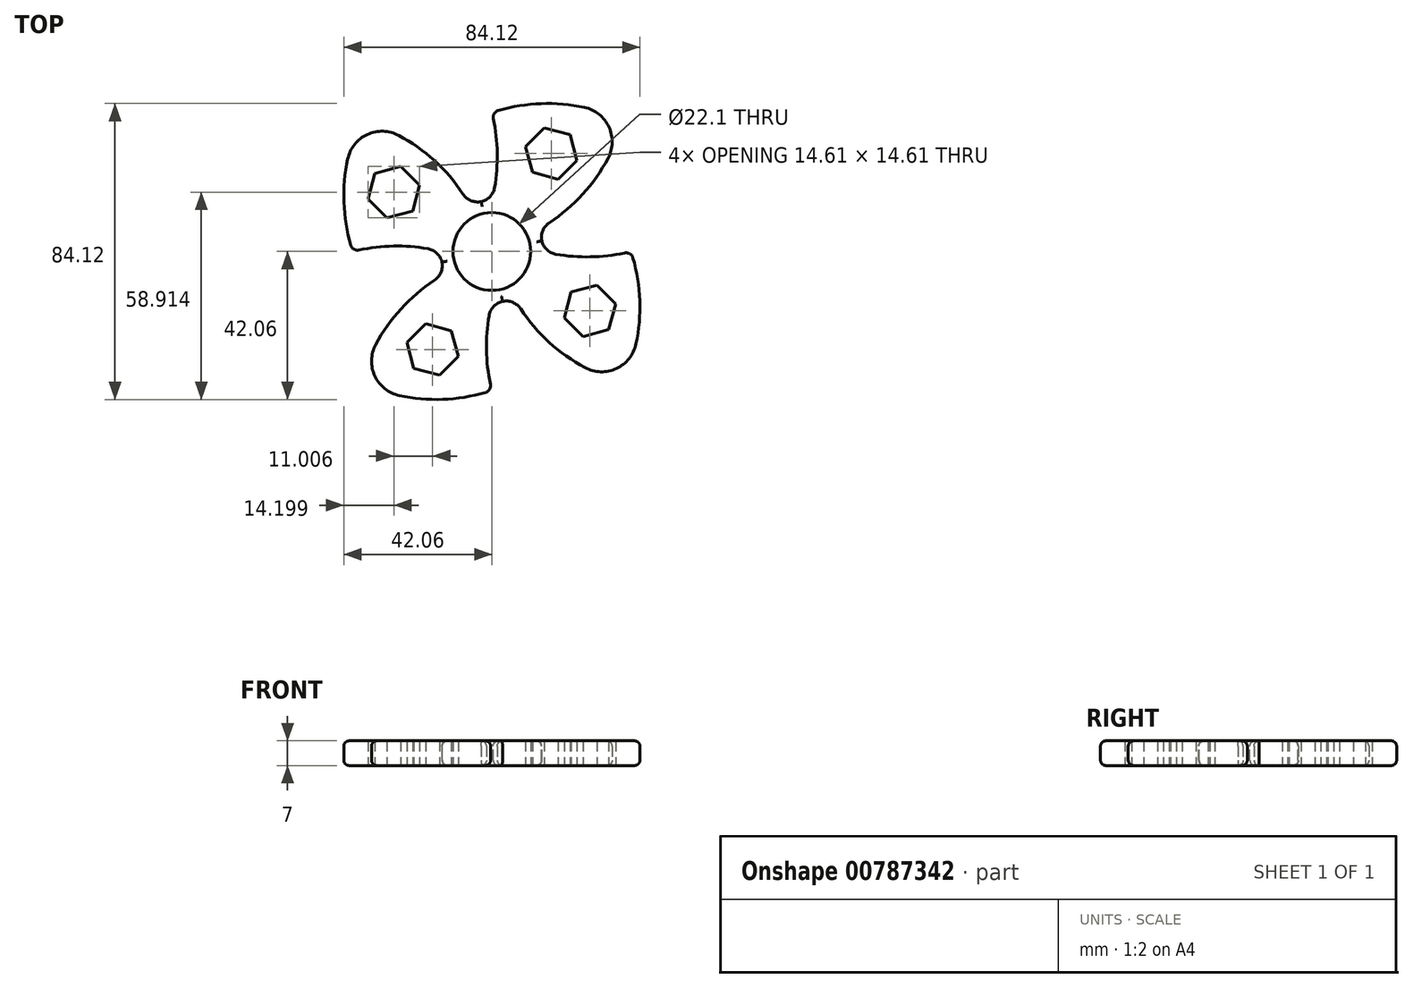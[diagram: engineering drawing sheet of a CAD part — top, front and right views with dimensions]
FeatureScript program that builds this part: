
annotation { "Feature Type Name" : "Feature", "Feature Type Description" : "" }
export const myFeature = defineFeature(function(context is Context, id is Id, definition is map)
    precondition{}
    {
        {
            var Q0;
            Q0=qCreatedBy(makeId("Top.planeOp"),FACE);
            var sketch = newSketch(context, id + "F0", { "sketchPlane" : qUnion([Q0])});
            skCircle(sketch, "E0", {"center": v(0, 0) * mm, "radius": 14.5 * mm});
            skArc(sketch, "E1", {"start": v(0, 14.5) * mm, "mid": v(1.54, 27) * mm, "end": v(0, 39.5) * mm});
            skPoint(sketch, "E2", {"position": v(0, 14.5) * mm});
            skPoint(sketch, "E3", {"position": v(0, 39.5) * mm});
            skLineSegment(sketch, "E4", {"start": v(0, 0) * mm, "end": v(51.9, 51.9) * mm, "construction": true});
            skPoint(sketch, "E5", {"position": v(37.23, 37.23) * mm});
            skArc(sketch, "E6.trimOffspring", {"start": v(37.23, 37.23) * mm, "mid": v(18.84, 41.97) * mm, "end": v(0, 39.5) * mm});
            skArc(sketch, "E7.trimOffspring", {"start": v(13.09, 6.24) * mm, "mid": v(28.33, 19.27) * mm, "end": v(37.23, 37.23) * mm});
            skCircle(sketch, "E8", {"center": v(0, 0) * mm, "radius": 11.05 * mm});
            skCircle(sketch, "E9.cCircle", {"center": v(16.85, 27.86) * mm, "radius": 6.55 * mm, "construction": true});
            skLineSegment(sketch, "E9.0", {"start": v(24.16, 25.9) * mm, "end": v(18.81, 20.56) * mm});
            skLineSegment(sketch, "E9.1", {"start": v(18.81, 20.56) * mm, "end": v(11.5, 22.51) * mm});
            skLineSegment(sketch, "E9.2", {"start": v(11.5, 22.51) * mm, "end": v(9.55, 29.82) * mm});
            skLineSegment(sketch, "E9.3", {"start": v(9.55, 29.82) * mm, "end": v(14.9, 35.17) * mm});
            skLineSegment(sketch, "E9.4", {"start": v(14.9, 35.17) * mm, "end": v(22.2, 33.2) * mm});
            skLineSegment(sketch, "E9.5", {"start": v(22.2, 33.2) * mm, "end": v(24.16, 25.9) * mm});
            skPoint(sketch, "E9.0.midPoint", {"position": v(21.49, 23.23) * mm});
            skArc(sketch, "E10.1.0", {"start": v(-6.24, 13.09) * mm, "mid": v(-19.27, 28.33) * mm, "end": v(-37.23, 37.23) * mm});
            skArc(sketch, "E10.1.1", {"start": v(-14.5, 0) * mm, "mid": v(-27, 1.54) * mm, "end": v(-39.5, 0) * mm});
            skArc(sketch, "E10.1.2", {"start": v(-37.23, 37.23) * mm, "mid": v(-41.97, 18.84) * mm, "end": v(-39.5, 0) * mm});
            skPoint(sketch, "E10.1.3", {"position": v(-23.23, 21.49) * mm});
            skLineSegment(sketch, "E10.1.4", {"start": v(-22.51, 11.5) * mm, "end": v(-29.82, 9.55) * mm});
            skCircle(sketch, "E10.1.5", {"center": v(-27.86, 16.85) * mm, "radius": 6.55 * mm, "construction": true});
            skLineSegment(sketch, "E10.1.6", {"start": v(-33.2, 22.2) * mm, "end": v(-25.9, 24.16) * mm});
            skLineSegment(sketch, "E10.1.7", {"start": v(-29.82, 9.55) * mm, "end": v(-35.17, 14.9) * mm});
            skLineSegment(sketch, "E10.1.8", {"start": v(-35.17, 14.9) * mm, "end": v(-33.2, 22.2) * mm});
            skLineSegment(sketch, "E10.1.9", {"start": v(-20.56, 18.81) * mm, "end": v(-22.51, 11.5) * mm});
            skLineSegment(sketch, "E10.1.10", {"start": v(-25.9, 24.16) * mm, "end": v(-20.56, 18.81) * mm});
            skArc(sketch, "E10.2.0", {"start": v(-13.09, -6.24) * mm, "mid": v(-28.33, -19.27) * mm, "end": v(-37.23, -37.23) * mm});
            skArc(sketch, "E10.2.1", {"start": v(0, -14.5) * mm, "mid": v(-1.54, -27) * mm, "end": v(0, -39.5) * mm});
            skArc(sketch, "E10.2.2", {"start": v(-37.23, -37.23) * mm, "mid": v(-18.84, -41.97) * mm, "end": v(0, -39.5) * mm});
            skPoint(sketch, "E10.2.3", {"position": v(-21.49, -23.23) * mm});
            skLineSegment(sketch, "E10.2.4", {"start": v(-11.5, -22.51) * mm, "end": v(-9.55, -29.82) * mm});
            skCircle(sketch, "E10.2.5", {"center": v(-16.85, -27.86) * mm, "radius": 6.55 * mm, "construction": true});
            skLineSegment(sketch, "E10.2.6", {"start": v(-22.2, -33.2) * mm, "end": v(-24.16, -25.9) * mm});
            skLineSegment(sketch, "E10.2.7", {"start": v(-9.55, -29.82) * mm, "end": v(-14.9, -35.17) * mm});
            skLineSegment(sketch, "E10.2.8", {"start": v(-14.9, -35.17) * mm, "end": v(-22.2, -33.2) * mm});
            skLineSegment(sketch, "E10.2.9", {"start": v(-18.81, -20.56) * mm, "end": v(-11.5, -22.51) * mm});
            skLineSegment(sketch, "E10.2.10", {"start": v(-24.16, -25.9) * mm, "end": v(-18.81, -20.56) * mm});
            skArc(sketch, "E10.3.0", {"start": v(6.24, -13.09) * mm, "mid": v(19.27, -28.33) * mm, "end": v(37.23, -37.23) * mm});
            skArc(sketch, "E10.3.1", {"start": v(14.5, 0) * mm, "mid": v(27, -1.54) * mm, "end": v(39.5, 0) * mm});
            skArc(sketch, "E10.3.2", {"start": v(37.23, -37.23) * mm, "mid": v(41.97, -18.84) * mm, "end": v(39.5, 0) * mm});
            skPoint(sketch, "E10.3.3", {"position": v(23.23, -21.49) * mm});
            skLineSegment(sketch, "E10.3.4", {"start": v(22.51, -11.5) * mm, "end": v(29.82, -9.55) * mm});
            skCircle(sketch, "E10.3.5", {"center": v(27.86, -16.85) * mm, "radius": 6.55 * mm, "construction": true});
            skLineSegment(sketch, "E10.3.6", {"start": v(33.2, -22.2) * mm, "end": v(25.9, -24.16) * mm});
            skLineSegment(sketch, "E10.3.7", {"start": v(29.82, -9.55) * mm, "end": v(35.17, -14.9) * mm});
            skLineSegment(sketch, "E10.3.8", {"start": v(35.17, -14.9) * mm, "end": v(33.2, -22.2) * mm});
            skLineSegment(sketch, "E10.3.9", {"start": v(20.56, -18.81) * mm, "end": v(22.51, -11.5) * mm});
            skLineSegment(sketch, "E10.3.10", {"start": v(25.9, -24.16) * mm, "end": v(20.56, -18.81) * mm});
            skSolve(sketch);
        }
        {
            var Q0;
            Q0 = qSketchRegion(id + "F0", true);
            extrude(context, id + "F1", {"entities" : qUnion([Q0]), "depth" : 7 * mm, "offsetDistance" : 25 * mm});
        }
        {
            var Q0;
            Q0=makeQuery(id+"F1.opExtrude","SWEPT_EDGE",EDGE,{"disambiguationData":[OSD([sQuery(id+"F0.wireOp",EDGE,"E6.trimOffspring"),sQuery(id+"F0.wireOp",EDGE,"E7.trimOffspring")])]});
            var Q1;
            Q1=makeQuery(id+"F1.opExtrude","SWEPT_EDGE",EDGE,{"disambiguationData":[OSD([sQuery(id+"F0.wireOp",EDGE,"E10.1.0"),sQuery(id+"F0.wireOp",EDGE,"E10.1.2")])]});
            var Q2;
            Q2=makeQuery(id+"F1.opExtrude","SWEPT_EDGE",EDGE,{"disambiguationData":[OSD([sQuery(id+"F0.wireOp",EDGE,"E10.2.0"),sQuery(id+"F0.wireOp",EDGE,"E10.2.2")])]});
            var Q3;
            Q3=makeQuery(id+"F1.opExtrude","SWEPT_EDGE",EDGE,{"disambiguationData":[OSD([sQuery(id+"F0.wireOp",EDGE,"E10.3.0"),sQuery(id+"F0.wireOp",EDGE,"E10.3.2")])]});
            fillet(context, id + "F2", {"entities" : qUnion([Q0, Q1, Q2, Q3]), "radius" : 10 * mm, "tangentPropagation" : true, "allowEdgeOverflow" : false});
        }
        {
            var Q0;
            Q0=makeQuery(id+"FwcY3XiP80TZzvs_1.opPattern","COPY",EDGE,{"derivedFrom":makeQuery(id+"F1.opExtrude","SWEPT_EDGE",EDGE,{"disambiguationData":[OSD([sQuery(id+"F0.wireOp",EDGE,"E1"),sQuery(id+"F0.wireOp",EDGE,"E6.trimOffspring")])]}),"instanceName":"1"});
            var Q1;
            Q1=makeQuery(id+"F1.opExtrude","SWEPT_EDGE",EDGE,{"disambiguationData":[OSD([sQuery(id+"F0.wireOp",EDGE,"E1"),sQuery(id+"F0.wireOp",EDGE,"E6.trimOffspring")])]});
            var Q2;
            Q2=makeQuery(id+"FwcY3XiP80TZzvs_1.opPattern","COPY",EDGE,{"derivedFrom":makeQuery(id+"F1.opExtrude","SWEPT_EDGE",EDGE,{"disambiguationData":[OSD([sQuery(id+"F0.wireOp",EDGE,"E1"),sQuery(id+"F0.wireOp",EDGE,"E6.trimOffspring")])]}),"instanceName":"3"});
            var Q3;
            Q3=makeQuery(id+"FwcY3XiP80TZzvs_1.opPattern","COPY",EDGE,{"derivedFrom":makeQuery(id+"F1.opExtrude","SWEPT_EDGE",EDGE,{"disambiguationData":[OSD([sQuery(id+"F0.wireOp",EDGE,"E1"),sQuery(id+"F0.wireOp",EDGE,"E6.trimOffspring")])]}),"instanceName":"2"});
            var Q4;
            Q4=makeQuery(id+"F1.opExtrude","SWEPT_EDGE",EDGE,{"disambiguationData":[OSD([sQuery(id+"F0.wireOp",EDGE,"E10.1.1"),sQuery(id+"F0.wireOp",EDGE,"E10.1.2")])]});
            var Q5;
            Q5=makeQuery(id+"F1.opExtrude","SWEPT_EDGE",EDGE,{"disambiguationData":[OSD([sQuery(id+"F0.wireOp",EDGE,"E10.2.1"),sQuery(id+"F0.wireOp",EDGE,"E10.2.2")])]});
            var Q6;
            Q6=makeQuery(id+"F1.opExtrude","SWEPT_EDGE",EDGE,{"disambiguationData":[OSD([sQuery(id+"F0.wireOp",EDGE,"E10.3.1"),sQuery(id+"F0.wireOp",EDGE,"E10.3.2")])]});
            fillet(context, id + "F3", {"entities" : qUnion([Q0, Q1, Q2, Q3, Q4, Q5, Q6]), "radius" : 2 * mm, "tangentPropagation" : true, "allowEdgeOverflow" : false});
        }
        {
            var Q0;
            Q0=makeQuery(id+"F1.opExtrude","SWEPT_EDGE",EDGE,{"disambiguationData":[OSD([sQuery(id+"F0.wireOp",EDGE,"E0"),sQuery(id+"F0.wireOp",EDGE,"E1")])]});
            var Q1;
            Q1=makeQuery(id+"FwcY3XiP80TZzvs_1.opPattern","COPY",EDGE,{"derivedFrom":makeQuery(id+"F1.opExtrude","SWEPT_EDGE",EDGE,{"disambiguationData":[OSD([sQuery(id+"F0.wireOp",EDGE,"E0"),sQuery(id+"F0.wireOp",EDGE,"E7.trimOffspring")])]}),"instanceName":"1"});
            var Q2;
            Q2=makeQuery(id+"FwcY3XiP80TZzvs_1.opPattern","COPY",EDGE,{"derivedFrom":makeQuery(id+"F1.opExtrude","SWEPT_EDGE",EDGE,{"disambiguationData":[OSD([sQuery(id+"F0.wireOp",EDGE,"E0"),sQuery(id+"F0.wireOp",EDGE,"E1")])]}),"instanceName":"1"});
            var Q3;
            Q3=makeQuery(id+"FwcY3XiP80TZzvs_1.opPattern","COPY",EDGE,{"derivedFrom":makeQuery(id+"F1.opExtrude","SWEPT_EDGE",EDGE,{"disambiguationData":[OSD([sQuery(id+"F0.wireOp",EDGE,"E0"),sQuery(id+"F0.wireOp",EDGE,"E7.trimOffspring")])]}),"instanceName":"2"});
            var Q4;
            Q4=makeQuery(id+"FwcY3XiP80TZzvs_1.opPattern","COPY",EDGE,{"derivedFrom":makeQuery(id+"F1.opExtrude","SWEPT_EDGE",EDGE,{"disambiguationData":[OSD([sQuery(id+"F0.wireOp",EDGE,"E0"),sQuery(id+"F0.wireOp",EDGE,"E1")])]}),"instanceName":"2"});
            var Q5;
            Q5=makeQuery(id+"FwcY3XiP80TZzvs_1.opPattern","COPY",EDGE,{"derivedFrom":makeQuery(id+"F1.opExtrude","SWEPT_EDGE",EDGE,{"disambiguationData":[OSD([sQuery(id+"F0.wireOp",EDGE,"E0"),sQuery(id+"F0.wireOp",EDGE,"E7.trimOffspring")])]}),"instanceName":"3"});
            var Q6;
            Q6=makeQuery(id+"FwcY3XiP80TZzvs_1.opPattern","COPY",EDGE,{"derivedFrom":makeQuery(id+"F1.opExtrude","SWEPT_EDGE",EDGE,{"disambiguationData":[OSD([sQuery(id+"F0.wireOp",EDGE,"E0"),sQuery(id+"F0.wireOp",EDGE,"E1")])]}),"instanceName":"3"});
            var Q7;
            Q7=makeQuery(id+"F1.opExtrude","SWEPT_EDGE",EDGE,{"disambiguationData":[OSD([sQuery(id+"F0.wireOp",EDGE,"E0"),sQuery(id+"F0.wireOp",EDGE,"E7.trimOffspring")])]});
            var Q8;
            Q8=makeQuery(id+"F1.opExtrude","SWEPT_EDGE",EDGE,{"disambiguationData":[OSD([sQuery(id+"F0.wireOp",EDGE,"E0"),sQuery(id+"F0.wireOp",EDGE,"E10.3.1")])]});
            var Q9;
            Q9=makeQuery(id+"F1.opExtrude","SWEPT_EDGE",EDGE,{"disambiguationData":[OSD([sQuery(id+"F0.wireOp",EDGE,"E0"),sQuery(id+"F0.wireOp",EDGE,"E10.3.0")])]});
            var Q10;
            Q10=makeQuery(id+"F1.opExtrude","SWEPT_EDGE",EDGE,{"disambiguationData":[OSD([sQuery(id+"F0.wireOp",EDGE,"E0"),sQuery(id+"F0.wireOp",EDGE,"E10.2.1")])]});
            var Q11;
            Q11=makeQuery(id+"F1.opExtrude","SWEPT_EDGE",EDGE,{"disambiguationData":[OSD([sQuery(id+"F0.wireOp",EDGE,"E0"),sQuery(id+"F0.wireOp",EDGE,"E10.1.0")])]});
            var Q12;
            Q12=makeQuery(id+"F1.opExtrude","SWEPT_EDGE",EDGE,{"disambiguationData":[OSD([sQuery(id+"F0.wireOp",EDGE,"E0"),sQuery(id+"F0.wireOp",EDGE,"E10.1.1")])]});
            var Q13;
            Q13=makeQuery(id+"F1.opExtrude","SWEPT_EDGE",EDGE,{"disambiguationData":[OSD([sQuery(id+"F0.wireOp",EDGE,"E0"),sQuery(id+"F0.wireOp",EDGE,"E10.2.0")])]});
            fillet(context, id + "F4", {"entities" : qUnion([Q0, Q1, Q2, Q3, Q4, Q5, Q6, Q7, Q8, Q9, Q10, Q11, Q12, Q13]), "radius" : 5 * mm, "tangentPropagation" : true, "allowEdgeOverflow" : false});
        }
        {
            var Q0;
            Q0=makeQuery(id+"FwcY3XiP80TZzvs_1.opPattern","COPY",EDGE,{"derivedFrom":makeQuery(id+"F1.opExtrude","CAP_EDGE",EDGE,{"disambiguationData":[OSD([sQuery(id+"F0.wireOp",EDGE,"E6.trimOffspring")])],"isStart":false}),"instanceName":"1"});
            var Q1;
            Q1=makeQuery(id+"FwcY3XiP80TZzvs_1.opPattern","COPY",EDGE,{"derivedFrom":makeQuery(id+"F1.opExtrude","CAP_EDGE",EDGE,{"disambiguationData":[OSD([sQuery(id+"F0.wireOp",EDGE,"E6.trimOffspring")])],"isStart":false}),"instanceName":"3"});
            var Q2;
            Q2=makeQuery(id+"FwcY3XiP80TZzvs_1.opPattern","COPY",EDGE,{"derivedFrom":makeQuery(id+"F1.opExtrude","CAP_EDGE",EDGE,{"disambiguationData":[OSD([sQuery(id+"F0.wireOp",EDGE,"E6.trimOffspring")])],"isStart":false}),"instanceName":"2"});
            var Q3;
            Q3=makeQuery(id+"F1.opExtrude","CAP_EDGE",EDGE,{"disambiguationData":[OSD([sQuery(id+"F0.wireOp",EDGE,"E6.trimOffspring")])],"isStart":false});
            var Q4;
            Q4=makeQuery(id+"F1.opExtrude","CAP_EDGE",EDGE,{"disambiguationData":[OSD([sQuery(id+"F0.wireOp",EDGE,"E6.trimOffspring")])],"isStart":true});
            var Q5;
            Q5=makeQuery(id+"FwcY3XiP80TZzvs_1.opPattern","COPY",EDGE,{"derivedFrom":makeQuery(id+"F1.opExtrude","CAP_EDGE",EDGE,{"disambiguationData":[OSD([sQuery(id+"F0.wireOp",EDGE,"E6.trimOffspring")])],"isStart":true}),"instanceName":"3"});
            var Q6;
            Q6=makeQuery(id+"FwcY3XiP80TZzvs_1.opPattern","COPY",EDGE,{"derivedFrom":makeQuery(id+"F1.opExtrude","CAP_EDGE",EDGE,{"disambiguationData":[OSD([sQuery(id+"F0.wireOp",EDGE,"E6.trimOffspring")])],"isStart":true}),"instanceName":"1"});
            var Q7;
            Q7=makeQuery(id+"FwcY3XiP80TZzvs_1.opPattern","COPY",EDGE,{"derivedFrom":makeQuery(id+"F1.opExtrude","CAP_EDGE",EDGE,{"disambiguationData":[OSD([sQuery(id+"F0.wireOp",EDGE,"E6.trimOffspring")])],"isStart":true}),"instanceName":"2"});
            var Q8;
            {var subQ0=sQuery(id+"F0.wireOp",EDGE,"E10.1.2");var subQ1=sQuery(id+"F0.wireOp",EDGE,"E10.1.0");Q8=makeQuery(id+"F2.opFillet","BLEND_EDGE",EDGE,{"blendedFrom":[makeQuery(id+"F1.opExtrude","SWEPT_EDGE",EDGE,{"disambiguationData":[OSD([subQ1,subQ0])]}),makeQuery(id+"F1.opExtrude","CAP_FACE",FACE,{"disambiguationData":[OSD([sQuery(id+"F0.wireOp",EDGE,"E0"),sQuery(id+"F0.wireOp",EDGE,"E1"),sQuery(id+"F0.wireOp",EDGE,"E6.trimOffspring"),sQuery(id+"F0.wireOp",EDGE,"E7.trimOffspring"),sQuery(id+"F0.wireOp",EDGE,"E8"),sQuery(id+"F0.wireOp",EDGE,"E9.0"),sQuery(id+"F0.wireOp",EDGE,"E9.1"),sQuery(id+"F0.wireOp",EDGE,"E9.2"),sQuery(id+"F0.wireOp",EDGE,"E9.3"),sQuery(id+"F0.wireOp",EDGE,"E9.4"),sQuery(id+"F0.wireOp",EDGE,"E9.5"),subQ1,sQuery(id+"F0.wireOp",EDGE,"E10.1.1"),subQ0,sQuery(id+"F0.wireOp",EDGE,"E10.1.4"),sQuery(id+"F0.wireOp",EDGE,"E10.1.6"),sQuery(id+"F0.wireOp",EDGE,"E10.1.7"),sQuery(id+"F0.wireOp",EDGE,"E10.1.8"),sQuery(id+"F0.wireOp",EDGE,"E10.1.9"),sQuery(id+"F0.wireOp",EDGE,"E10.1.10"),sQuery(id+"F0.wireOp",EDGE,"E10.2.0"),sQuery(id+"F0.wireOp",EDGE,"E10.2.1"),sQuery(id+"F0.wireOp",EDGE,"E10.2.2"),sQuery(id+"F0.wireOp",EDGE,"E10.2.4"),sQuery(id+"F0.wireOp",EDGE,"E10.2.6"),sQuery(id+"F0.wireOp",EDGE,"E10.2.7"),sQuery(id+"F0.wireOp",EDGE,"E10.2.8"),sQuery(id+"F0.wireOp",EDGE,"E10.2.9"),sQuery(id+"F0.wireOp",EDGE,"E10.2.10"),sQuery(id+"F0.wireOp",EDGE,"E10.3.0"),sQuery(id+"F0.wireOp",EDGE,"E10.3.1"),sQuery(id+"F0.wireOp",EDGE,"E10.3.2"),sQuery(id+"F0.wireOp",EDGE,"E10.3.4"),sQuery(id+"F0.wireOp",EDGE,"E10.3.6"),sQuery(id+"F0.wireOp",EDGE,"E10.3.7"),sQuery(id+"F0.wireOp",EDGE,"E10.3.8"),sQuery(id+"F0.wireOp",EDGE,"E10.3.9"),sQuery(id+"F0.wireOp",EDGE,"E10.3.10")])],"isStart":true})],"blendedInto":[makeQuery(id+"F1.opExtrude","CAP_FACE",FACE,{"disambiguationData":[OSD([sQuery(id+"F0.wireOp",EDGE,"E0"),sQuery(id+"F0.wireOp",EDGE,"E1"),sQuery(id+"F0.wireOp",EDGE,"E6.trimOffspring"),sQuery(id+"F0.wireOp",EDGE,"E7.trimOffspring"),sQuery(id+"F0.wireOp",EDGE,"E8"),sQuery(id+"F0.wireOp",EDGE,"E9.0"),sQuery(id+"F0.wireOp",EDGE,"E9.1"),sQuery(id+"F0.wireOp",EDGE,"E9.2"),sQuery(id+"F0.wireOp",EDGE,"E9.3"),sQuery(id+"F0.wireOp",EDGE,"E9.4"),sQuery(id+"F0.wireOp",EDGE,"E9.5"),subQ1,sQuery(id+"F0.wireOp",EDGE,"E10.1.1"),subQ0,sQuery(id+"F0.wireOp",EDGE,"E10.1.4"),sQuery(id+"F0.wireOp",EDGE,"E10.1.6"),sQuery(id+"F0.wireOp",EDGE,"E10.1.7"),sQuery(id+"F0.wireOp",EDGE,"E10.1.8"),sQuery(id+"F0.wireOp",EDGE,"E10.1.9"),sQuery(id+"F0.wireOp",EDGE,"E10.1.10"),sQuery(id+"F0.wireOp",EDGE,"E10.2.0"),sQuery(id+"F0.wireOp",EDGE,"E10.2.1"),sQuery(id+"F0.wireOp",EDGE,"E10.2.2"),sQuery(id+"F0.wireOp",EDGE,"E10.2.4"),sQuery(id+"F0.wireOp",EDGE,"E10.2.6"),sQuery(id+"F0.wireOp",EDGE,"E10.2.7"),sQuery(id+"F0.wireOp",EDGE,"E10.2.8"),sQuery(id+"F0.wireOp",EDGE,"E10.2.9"),sQuery(id+"F0.wireOp",EDGE,"E10.2.10"),sQuery(id+"F0.wireOp",EDGE,"E10.3.0"),sQuery(id+"F0.wireOp",EDGE,"E10.3.1"),sQuery(id+"F0.wireOp",EDGE,"E10.3.2"),sQuery(id+"F0.wireOp",EDGE,"E10.3.4"),sQuery(id+"F0.wireOp",EDGE,"E10.3.6"),sQuery(id+"F0.wireOp",EDGE,"E10.3.7"),sQuery(id+"F0.wireOp",EDGE,"E10.3.8"),sQuery(id+"F0.wireOp",EDGE,"E10.3.9"),sQuery(id+"F0.wireOp",EDGE,"E10.3.10")])],"isStart":true})]});}
            var Q9;
            {var subQ0=sQuery(id+"F0.wireOp",EDGE,"E10.2.2");var subQ1=sQuery(id+"F0.wireOp",EDGE,"E10.2.0");Q9=makeQuery(id+"F2.opFillet","BLEND_EDGE",EDGE,{"blendedFrom":[makeQuery(id+"F1.opExtrude","SWEPT_EDGE",EDGE,{"disambiguationData":[OSD([subQ1,subQ0])]}),makeQuery(id+"F1.opExtrude","CAP_FACE",FACE,{"disambiguationData":[OSD([sQuery(id+"F0.wireOp",EDGE,"E0"),sQuery(id+"F0.wireOp",EDGE,"E1"),sQuery(id+"F0.wireOp",EDGE,"E6.trimOffspring"),sQuery(id+"F0.wireOp",EDGE,"E7.trimOffspring"),sQuery(id+"F0.wireOp",EDGE,"E8"),sQuery(id+"F0.wireOp",EDGE,"E9.0"),sQuery(id+"F0.wireOp",EDGE,"E9.1"),sQuery(id+"F0.wireOp",EDGE,"E9.2"),sQuery(id+"F0.wireOp",EDGE,"E9.3"),sQuery(id+"F0.wireOp",EDGE,"E9.4"),sQuery(id+"F0.wireOp",EDGE,"E9.5"),sQuery(id+"F0.wireOp",EDGE,"E10.1.0"),sQuery(id+"F0.wireOp",EDGE,"E10.1.1"),sQuery(id+"F0.wireOp",EDGE,"E10.1.2"),sQuery(id+"F0.wireOp",EDGE,"E10.1.4"),sQuery(id+"F0.wireOp",EDGE,"E10.1.6"),sQuery(id+"F0.wireOp",EDGE,"E10.1.7"),sQuery(id+"F0.wireOp",EDGE,"E10.1.8"),sQuery(id+"F0.wireOp",EDGE,"E10.1.9"),sQuery(id+"F0.wireOp",EDGE,"E10.1.10"),subQ1,sQuery(id+"F0.wireOp",EDGE,"E10.2.1"),subQ0,sQuery(id+"F0.wireOp",EDGE,"E10.2.4"),sQuery(id+"F0.wireOp",EDGE,"E10.2.6"),sQuery(id+"F0.wireOp",EDGE,"E10.2.7"),sQuery(id+"F0.wireOp",EDGE,"E10.2.8"),sQuery(id+"F0.wireOp",EDGE,"E10.2.9"),sQuery(id+"F0.wireOp",EDGE,"E10.2.10"),sQuery(id+"F0.wireOp",EDGE,"E10.3.0"),sQuery(id+"F0.wireOp",EDGE,"E10.3.1"),sQuery(id+"F0.wireOp",EDGE,"E10.3.2"),sQuery(id+"F0.wireOp",EDGE,"E10.3.4"),sQuery(id+"F0.wireOp",EDGE,"E10.3.6"),sQuery(id+"F0.wireOp",EDGE,"E10.3.7"),sQuery(id+"F0.wireOp",EDGE,"E10.3.8"),sQuery(id+"F0.wireOp",EDGE,"E10.3.9"),sQuery(id+"F0.wireOp",EDGE,"E10.3.10")])],"isStart":true})],"blendedInto":[makeQuery(id+"F1.opExtrude","CAP_FACE",FACE,{"disambiguationData":[OSD([sQuery(id+"F0.wireOp",EDGE,"E0"),sQuery(id+"F0.wireOp",EDGE,"E1"),sQuery(id+"F0.wireOp",EDGE,"E6.trimOffspring"),sQuery(id+"F0.wireOp",EDGE,"E7.trimOffspring"),sQuery(id+"F0.wireOp",EDGE,"E8"),sQuery(id+"F0.wireOp",EDGE,"E9.0"),sQuery(id+"F0.wireOp",EDGE,"E9.1"),sQuery(id+"F0.wireOp",EDGE,"E9.2"),sQuery(id+"F0.wireOp",EDGE,"E9.3"),sQuery(id+"F0.wireOp",EDGE,"E9.4"),sQuery(id+"F0.wireOp",EDGE,"E9.5"),sQuery(id+"F0.wireOp",EDGE,"E10.1.0"),sQuery(id+"F0.wireOp",EDGE,"E10.1.1"),sQuery(id+"F0.wireOp",EDGE,"E10.1.2"),sQuery(id+"F0.wireOp",EDGE,"E10.1.4"),sQuery(id+"F0.wireOp",EDGE,"E10.1.6"),sQuery(id+"F0.wireOp",EDGE,"E10.1.7"),sQuery(id+"F0.wireOp",EDGE,"E10.1.8"),sQuery(id+"F0.wireOp",EDGE,"E10.1.9"),sQuery(id+"F0.wireOp",EDGE,"E10.1.10"),subQ1,sQuery(id+"F0.wireOp",EDGE,"E10.2.1"),subQ0,sQuery(id+"F0.wireOp",EDGE,"E10.2.4"),sQuery(id+"F0.wireOp",EDGE,"E10.2.6"),sQuery(id+"F0.wireOp",EDGE,"E10.2.7"),sQuery(id+"F0.wireOp",EDGE,"E10.2.8"),sQuery(id+"F0.wireOp",EDGE,"E10.2.9"),sQuery(id+"F0.wireOp",EDGE,"E10.2.10"),sQuery(id+"F0.wireOp",EDGE,"E10.3.0"),sQuery(id+"F0.wireOp",EDGE,"E10.3.1"),sQuery(id+"F0.wireOp",EDGE,"E10.3.2"),sQuery(id+"F0.wireOp",EDGE,"E10.3.4"),sQuery(id+"F0.wireOp",EDGE,"E10.3.6"),sQuery(id+"F0.wireOp",EDGE,"E10.3.7"),sQuery(id+"F0.wireOp",EDGE,"E10.3.8"),sQuery(id+"F0.wireOp",EDGE,"E10.3.9"),sQuery(id+"F0.wireOp",EDGE,"E10.3.10")])],"isStart":true})]});}
            var Q10;
            {var subQ0=sQuery(id+"F0.wireOp",EDGE,"E10.3.2");var subQ1=sQuery(id+"F0.wireOp",EDGE,"E10.3.0");Q10=makeQuery(id+"F2.opFillet","BLEND_EDGE",EDGE,{"blendedFrom":[makeQuery(id+"F1.opExtrude","SWEPT_EDGE",EDGE,{"disambiguationData":[OSD([subQ1,subQ0])]}),makeQuery(id+"F1.opExtrude","CAP_FACE",FACE,{"disambiguationData":[OSD([sQuery(id+"F0.wireOp",EDGE,"E0"),sQuery(id+"F0.wireOp",EDGE,"E1"),sQuery(id+"F0.wireOp",EDGE,"E6.trimOffspring"),sQuery(id+"F0.wireOp",EDGE,"E7.trimOffspring"),sQuery(id+"F0.wireOp",EDGE,"E8"),sQuery(id+"F0.wireOp",EDGE,"E9.0"),sQuery(id+"F0.wireOp",EDGE,"E9.1"),sQuery(id+"F0.wireOp",EDGE,"E9.2"),sQuery(id+"F0.wireOp",EDGE,"E9.3"),sQuery(id+"F0.wireOp",EDGE,"E9.4"),sQuery(id+"F0.wireOp",EDGE,"E9.5"),sQuery(id+"F0.wireOp",EDGE,"E10.1.0"),sQuery(id+"F0.wireOp",EDGE,"E10.1.1"),sQuery(id+"F0.wireOp",EDGE,"E10.1.2"),sQuery(id+"F0.wireOp",EDGE,"E10.1.4"),sQuery(id+"F0.wireOp",EDGE,"E10.1.6"),sQuery(id+"F0.wireOp",EDGE,"E10.1.7"),sQuery(id+"F0.wireOp",EDGE,"E10.1.8"),sQuery(id+"F0.wireOp",EDGE,"E10.1.9"),sQuery(id+"F0.wireOp",EDGE,"E10.1.10"),sQuery(id+"F0.wireOp",EDGE,"E10.2.0"),sQuery(id+"F0.wireOp",EDGE,"E10.2.1"),sQuery(id+"F0.wireOp",EDGE,"E10.2.2"),sQuery(id+"F0.wireOp",EDGE,"E10.2.4"),sQuery(id+"F0.wireOp",EDGE,"E10.2.6"),sQuery(id+"F0.wireOp",EDGE,"E10.2.7"),sQuery(id+"F0.wireOp",EDGE,"E10.2.8"),sQuery(id+"F0.wireOp",EDGE,"E10.2.9"),sQuery(id+"F0.wireOp",EDGE,"E10.2.10"),subQ1,sQuery(id+"F0.wireOp",EDGE,"E10.3.1"),subQ0,sQuery(id+"F0.wireOp",EDGE,"E10.3.4"),sQuery(id+"F0.wireOp",EDGE,"E10.3.6"),sQuery(id+"F0.wireOp",EDGE,"E10.3.7"),sQuery(id+"F0.wireOp",EDGE,"E10.3.8"),sQuery(id+"F0.wireOp",EDGE,"E10.3.9"),sQuery(id+"F0.wireOp",EDGE,"E10.3.10")])],"isStart":true})],"blendedInto":[makeQuery(id+"F1.opExtrude","CAP_FACE",FACE,{"disambiguationData":[OSD([sQuery(id+"F0.wireOp",EDGE,"E0"),sQuery(id+"F0.wireOp",EDGE,"E1"),sQuery(id+"F0.wireOp",EDGE,"E6.trimOffspring"),sQuery(id+"F0.wireOp",EDGE,"E7.trimOffspring"),sQuery(id+"F0.wireOp",EDGE,"E8"),sQuery(id+"F0.wireOp",EDGE,"E9.0"),sQuery(id+"F0.wireOp",EDGE,"E9.1"),sQuery(id+"F0.wireOp",EDGE,"E9.2"),sQuery(id+"F0.wireOp",EDGE,"E9.3"),sQuery(id+"F0.wireOp",EDGE,"E9.4"),sQuery(id+"F0.wireOp",EDGE,"E9.5"),sQuery(id+"F0.wireOp",EDGE,"E10.1.0"),sQuery(id+"F0.wireOp",EDGE,"E10.1.1"),sQuery(id+"F0.wireOp",EDGE,"E10.1.2"),sQuery(id+"F0.wireOp",EDGE,"E10.1.4"),sQuery(id+"F0.wireOp",EDGE,"E10.1.6"),sQuery(id+"F0.wireOp",EDGE,"E10.1.7"),sQuery(id+"F0.wireOp",EDGE,"E10.1.8"),sQuery(id+"F0.wireOp",EDGE,"E10.1.9"),sQuery(id+"F0.wireOp",EDGE,"E10.1.10"),sQuery(id+"F0.wireOp",EDGE,"E10.2.0"),sQuery(id+"F0.wireOp",EDGE,"E10.2.1"),sQuery(id+"F0.wireOp",EDGE,"E10.2.2"),sQuery(id+"F0.wireOp",EDGE,"E10.2.4"),sQuery(id+"F0.wireOp",EDGE,"E10.2.6"),sQuery(id+"F0.wireOp",EDGE,"E10.2.7"),sQuery(id+"F0.wireOp",EDGE,"E10.2.8"),sQuery(id+"F0.wireOp",EDGE,"E10.2.9"),sQuery(id+"F0.wireOp",EDGE,"E10.2.10"),subQ1,sQuery(id+"F0.wireOp",EDGE,"E10.3.1"),subQ0,sQuery(id+"F0.wireOp",EDGE,"E10.3.4"),sQuery(id+"F0.wireOp",EDGE,"E10.3.6"),sQuery(id+"F0.wireOp",EDGE,"E10.3.7"),sQuery(id+"F0.wireOp",EDGE,"E10.3.8"),sQuery(id+"F0.wireOp",EDGE,"E10.3.9"),sQuery(id+"F0.wireOp",EDGE,"E10.3.10")])],"isStart":true})]});}
            var Q11;
            {var subQ0=sQuery(id+"F0.wireOp",EDGE,"E10.3.2");var subQ1=sQuery(id+"F0.wireOp",EDGE,"E10.3.0");Q11=makeQuery(id+"F2.opFillet","BLEND_EDGE",EDGE,{"blendedFrom":[makeQuery(id+"F1.opExtrude","SWEPT_EDGE",EDGE,{"disambiguationData":[OSD([subQ1,subQ0])]}),makeQuery(id+"F1.opExtrude","CAP_FACE",FACE,{"disambiguationData":[OSD([sQuery(id+"F0.wireOp",EDGE,"E0"),sQuery(id+"F0.wireOp",EDGE,"E1"),sQuery(id+"F0.wireOp",EDGE,"E6.trimOffspring"),sQuery(id+"F0.wireOp",EDGE,"E7.trimOffspring"),sQuery(id+"F0.wireOp",EDGE,"E8"),sQuery(id+"F0.wireOp",EDGE,"E9.0"),sQuery(id+"F0.wireOp",EDGE,"E9.1"),sQuery(id+"F0.wireOp",EDGE,"E9.2"),sQuery(id+"F0.wireOp",EDGE,"E9.3"),sQuery(id+"F0.wireOp",EDGE,"E9.4"),sQuery(id+"F0.wireOp",EDGE,"E9.5"),sQuery(id+"F0.wireOp",EDGE,"E10.1.0"),sQuery(id+"F0.wireOp",EDGE,"E10.1.1"),sQuery(id+"F0.wireOp",EDGE,"E10.1.2"),sQuery(id+"F0.wireOp",EDGE,"E10.1.4"),sQuery(id+"F0.wireOp",EDGE,"E10.1.6"),sQuery(id+"F0.wireOp",EDGE,"E10.1.7"),sQuery(id+"F0.wireOp",EDGE,"E10.1.8"),sQuery(id+"F0.wireOp",EDGE,"E10.1.9"),sQuery(id+"F0.wireOp",EDGE,"E10.1.10"),sQuery(id+"F0.wireOp",EDGE,"E10.2.0"),sQuery(id+"F0.wireOp",EDGE,"E10.2.1"),sQuery(id+"F0.wireOp",EDGE,"E10.2.2"),sQuery(id+"F0.wireOp",EDGE,"E10.2.4"),sQuery(id+"F0.wireOp",EDGE,"E10.2.6"),sQuery(id+"F0.wireOp",EDGE,"E10.2.7"),sQuery(id+"F0.wireOp",EDGE,"E10.2.8"),sQuery(id+"F0.wireOp",EDGE,"E10.2.9"),sQuery(id+"F0.wireOp",EDGE,"E10.2.10"),subQ1,sQuery(id+"F0.wireOp",EDGE,"E10.3.1"),subQ0,sQuery(id+"F0.wireOp",EDGE,"E10.3.4"),sQuery(id+"F0.wireOp",EDGE,"E10.3.6"),sQuery(id+"F0.wireOp",EDGE,"E10.3.7"),sQuery(id+"F0.wireOp",EDGE,"E10.3.8"),sQuery(id+"F0.wireOp",EDGE,"E10.3.9"),sQuery(id+"F0.wireOp",EDGE,"E10.3.10")])],"isStart":false})],"blendedInto":[makeQuery(id+"F1.opExtrude","CAP_FACE",FACE,{"disambiguationData":[OSD([sQuery(id+"F0.wireOp",EDGE,"E0"),sQuery(id+"F0.wireOp",EDGE,"E1"),sQuery(id+"F0.wireOp",EDGE,"E6.trimOffspring"),sQuery(id+"F0.wireOp",EDGE,"E7.trimOffspring"),sQuery(id+"F0.wireOp",EDGE,"E8"),sQuery(id+"F0.wireOp",EDGE,"E9.0"),sQuery(id+"F0.wireOp",EDGE,"E9.1"),sQuery(id+"F0.wireOp",EDGE,"E9.2"),sQuery(id+"F0.wireOp",EDGE,"E9.3"),sQuery(id+"F0.wireOp",EDGE,"E9.4"),sQuery(id+"F0.wireOp",EDGE,"E9.5"),sQuery(id+"F0.wireOp",EDGE,"E10.1.0"),sQuery(id+"F0.wireOp",EDGE,"E10.1.1"),sQuery(id+"F0.wireOp",EDGE,"E10.1.2"),sQuery(id+"F0.wireOp",EDGE,"E10.1.4"),sQuery(id+"F0.wireOp",EDGE,"E10.1.6"),sQuery(id+"F0.wireOp",EDGE,"E10.1.7"),sQuery(id+"F0.wireOp",EDGE,"E10.1.8"),sQuery(id+"F0.wireOp",EDGE,"E10.1.9"),sQuery(id+"F0.wireOp",EDGE,"E10.1.10"),sQuery(id+"F0.wireOp",EDGE,"E10.2.0"),sQuery(id+"F0.wireOp",EDGE,"E10.2.1"),sQuery(id+"F0.wireOp",EDGE,"E10.2.2"),sQuery(id+"F0.wireOp",EDGE,"E10.2.4"),sQuery(id+"F0.wireOp",EDGE,"E10.2.6"),sQuery(id+"F0.wireOp",EDGE,"E10.2.7"),sQuery(id+"F0.wireOp",EDGE,"E10.2.8"),sQuery(id+"F0.wireOp",EDGE,"E10.2.9"),sQuery(id+"F0.wireOp",EDGE,"E10.2.10"),subQ1,sQuery(id+"F0.wireOp",EDGE,"E10.3.1"),subQ0,sQuery(id+"F0.wireOp",EDGE,"E10.3.4"),sQuery(id+"F0.wireOp",EDGE,"E10.3.6"),sQuery(id+"F0.wireOp",EDGE,"E10.3.7"),sQuery(id+"F0.wireOp",EDGE,"E10.3.8"),sQuery(id+"F0.wireOp",EDGE,"E10.3.9"),sQuery(id+"F0.wireOp",EDGE,"E10.3.10")])],"isStart":false})]});}
            var Q12;
            {var subQ0=sQuery(id+"F0.wireOp",EDGE,"E10.2.2");var subQ1=sQuery(id+"F0.wireOp",EDGE,"E10.2.0");Q12=makeQuery(id+"F2.opFillet","BLEND_EDGE",EDGE,{"blendedFrom":[makeQuery(id+"F1.opExtrude","SWEPT_EDGE",EDGE,{"disambiguationData":[OSD([subQ1,subQ0])]}),makeQuery(id+"F1.opExtrude","CAP_FACE",FACE,{"disambiguationData":[OSD([sQuery(id+"F0.wireOp",EDGE,"E0"),sQuery(id+"F0.wireOp",EDGE,"E1"),sQuery(id+"F0.wireOp",EDGE,"E6.trimOffspring"),sQuery(id+"F0.wireOp",EDGE,"E7.trimOffspring"),sQuery(id+"F0.wireOp",EDGE,"E8"),sQuery(id+"F0.wireOp",EDGE,"E9.0"),sQuery(id+"F0.wireOp",EDGE,"E9.1"),sQuery(id+"F0.wireOp",EDGE,"E9.2"),sQuery(id+"F0.wireOp",EDGE,"E9.3"),sQuery(id+"F0.wireOp",EDGE,"E9.4"),sQuery(id+"F0.wireOp",EDGE,"E9.5"),sQuery(id+"F0.wireOp",EDGE,"E10.1.0"),sQuery(id+"F0.wireOp",EDGE,"E10.1.1"),sQuery(id+"F0.wireOp",EDGE,"E10.1.2"),sQuery(id+"F0.wireOp",EDGE,"E10.1.4"),sQuery(id+"F0.wireOp",EDGE,"E10.1.6"),sQuery(id+"F0.wireOp",EDGE,"E10.1.7"),sQuery(id+"F0.wireOp",EDGE,"E10.1.8"),sQuery(id+"F0.wireOp",EDGE,"E10.1.9"),sQuery(id+"F0.wireOp",EDGE,"E10.1.10"),subQ1,sQuery(id+"F0.wireOp",EDGE,"E10.2.1"),subQ0,sQuery(id+"F0.wireOp",EDGE,"E10.2.4"),sQuery(id+"F0.wireOp",EDGE,"E10.2.6"),sQuery(id+"F0.wireOp",EDGE,"E10.2.7"),sQuery(id+"F0.wireOp",EDGE,"E10.2.8"),sQuery(id+"F0.wireOp",EDGE,"E10.2.9"),sQuery(id+"F0.wireOp",EDGE,"E10.2.10"),sQuery(id+"F0.wireOp",EDGE,"E10.3.0"),sQuery(id+"F0.wireOp",EDGE,"E10.3.1"),sQuery(id+"F0.wireOp",EDGE,"E10.3.2"),sQuery(id+"F0.wireOp",EDGE,"E10.3.4"),sQuery(id+"F0.wireOp",EDGE,"E10.3.6"),sQuery(id+"F0.wireOp",EDGE,"E10.3.7"),sQuery(id+"F0.wireOp",EDGE,"E10.3.8"),sQuery(id+"F0.wireOp",EDGE,"E10.3.9"),sQuery(id+"F0.wireOp",EDGE,"E10.3.10")])],"isStart":false})],"blendedInto":[makeQuery(id+"F1.opExtrude","CAP_FACE",FACE,{"disambiguationData":[OSD([sQuery(id+"F0.wireOp",EDGE,"E0"),sQuery(id+"F0.wireOp",EDGE,"E1"),sQuery(id+"F0.wireOp",EDGE,"E6.trimOffspring"),sQuery(id+"F0.wireOp",EDGE,"E7.trimOffspring"),sQuery(id+"F0.wireOp",EDGE,"E8"),sQuery(id+"F0.wireOp",EDGE,"E9.0"),sQuery(id+"F0.wireOp",EDGE,"E9.1"),sQuery(id+"F0.wireOp",EDGE,"E9.2"),sQuery(id+"F0.wireOp",EDGE,"E9.3"),sQuery(id+"F0.wireOp",EDGE,"E9.4"),sQuery(id+"F0.wireOp",EDGE,"E9.5"),sQuery(id+"F0.wireOp",EDGE,"E10.1.0"),sQuery(id+"F0.wireOp",EDGE,"E10.1.1"),sQuery(id+"F0.wireOp",EDGE,"E10.1.2"),sQuery(id+"F0.wireOp",EDGE,"E10.1.4"),sQuery(id+"F0.wireOp",EDGE,"E10.1.6"),sQuery(id+"F0.wireOp",EDGE,"E10.1.7"),sQuery(id+"F0.wireOp",EDGE,"E10.1.8"),sQuery(id+"F0.wireOp",EDGE,"E10.1.9"),sQuery(id+"F0.wireOp",EDGE,"E10.1.10"),subQ1,sQuery(id+"F0.wireOp",EDGE,"E10.2.1"),subQ0,sQuery(id+"F0.wireOp",EDGE,"E10.2.4"),sQuery(id+"F0.wireOp",EDGE,"E10.2.6"),sQuery(id+"F0.wireOp",EDGE,"E10.2.7"),sQuery(id+"F0.wireOp",EDGE,"E10.2.8"),sQuery(id+"F0.wireOp",EDGE,"E10.2.9"),sQuery(id+"F0.wireOp",EDGE,"E10.2.10"),sQuery(id+"F0.wireOp",EDGE,"E10.3.0"),sQuery(id+"F0.wireOp",EDGE,"E10.3.1"),sQuery(id+"F0.wireOp",EDGE,"E10.3.2"),sQuery(id+"F0.wireOp",EDGE,"E10.3.4"),sQuery(id+"F0.wireOp",EDGE,"E10.3.6"),sQuery(id+"F0.wireOp",EDGE,"E10.3.7"),sQuery(id+"F0.wireOp",EDGE,"E10.3.8"),sQuery(id+"F0.wireOp",EDGE,"E10.3.9"),sQuery(id+"F0.wireOp",EDGE,"E10.3.10")])],"isStart":false})]});}
            var Q13;
            {var subQ0=sQuery(id+"F0.wireOp",EDGE,"E10.1.2");var subQ1=sQuery(id+"F0.wireOp",EDGE,"E10.1.0");Q13=makeQuery(id+"F2.opFillet","BLEND_EDGE",EDGE,{"blendedFrom":[makeQuery(id+"F1.opExtrude","SWEPT_EDGE",EDGE,{"disambiguationData":[OSD([subQ1,subQ0])]}),makeQuery(id+"F1.opExtrude","CAP_FACE",FACE,{"disambiguationData":[OSD([sQuery(id+"F0.wireOp",EDGE,"E0"),sQuery(id+"F0.wireOp",EDGE,"E1"),sQuery(id+"F0.wireOp",EDGE,"E6.trimOffspring"),sQuery(id+"F0.wireOp",EDGE,"E7.trimOffspring"),sQuery(id+"F0.wireOp",EDGE,"E8"),sQuery(id+"F0.wireOp",EDGE,"E9.0"),sQuery(id+"F0.wireOp",EDGE,"E9.1"),sQuery(id+"F0.wireOp",EDGE,"E9.2"),sQuery(id+"F0.wireOp",EDGE,"E9.3"),sQuery(id+"F0.wireOp",EDGE,"E9.4"),sQuery(id+"F0.wireOp",EDGE,"E9.5"),subQ1,sQuery(id+"F0.wireOp",EDGE,"E10.1.1"),subQ0,sQuery(id+"F0.wireOp",EDGE,"E10.1.4"),sQuery(id+"F0.wireOp",EDGE,"E10.1.6"),sQuery(id+"F0.wireOp",EDGE,"E10.1.7"),sQuery(id+"F0.wireOp",EDGE,"E10.1.8"),sQuery(id+"F0.wireOp",EDGE,"E10.1.9"),sQuery(id+"F0.wireOp",EDGE,"E10.1.10"),sQuery(id+"F0.wireOp",EDGE,"E10.2.0"),sQuery(id+"F0.wireOp",EDGE,"E10.2.1"),sQuery(id+"F0.wireOp",EDGE,"E10.2.2"),sQuery(id+"F0.wireOp",EDGE,"E10.2.4"),sQuery(id+"F0.wireOp",EDGE,"E10.2.6"),sQuery(id+"F0.wireOp",EDGE,"E10.2.7"),sQuery(id+"F0.wireOp",EDGE,"E10.2.8"),sQuery(id+"F0.wireOp",EDGE,"E10.2.9"),sQuery(id+"F0.wireOp",EDGE,"E10.2.10"),sQuery(id+"F0.wireOp",EDGE,"E10.3.0"),sQuery(id+"F0.wireOp",EDGE,"E10.3.1"),sQuery(id+"F0.wireOp",EDGE,"E10.3.2"),sQuery(id+"F0.wireOp",EDGE,"E10.3.4"),sQuery(id+"F0.wireOp",EDGE,"E10.3.6"),sQuery(id+"F0.wireOp",EDGE,"E10.3.7"),sQuery(id+"F0.wireOp",EDGE,"E10.3.8"),sQuery(id+"F0.wireOp",EDGE,"E10.3.9"),sQuery(id+"F0.wireOp",EDGE,"E10.3.10")])],"isStart":false})],"blendedInto":[makeQuery(id+"F1.opExtrude","CAP_FACE",FACE,{"disambiguationData":[OSD([sQuery(id+"F0.wireOp",EDGE,"E0"),sQuery(id+"F0.wireOp",EDGE,"E1"),sQuery(id+"F0.wireOp",EDGE,"E6.trimOffspring"),sQuery(id+"F0.wireOp",EDGE,"E7.trimOffspring"),sQuery(id+"F0.wireOp",EDGE,"E8"),sQuery(id+"F0.wireOp",EDGE,"E9.0"),sQuery(id+"F0.wireOp",EDGE,"E9.1"),sQuery(id+"F0.wireOp",EDGE,"E9.2"),sQuery(id+"F0.wireOp",EDGE,"E9.3"),sQuery(id+"F0.wireOp",EDGE,"E9.4"),sQuery(id+"F0.wireOp",EDGE,"E9.5"),subQ1,sQuery(id+"F0.wireOp",EDGE,"E10.1.1"),subQ0,sQuery(id+"F0.wireOp",EDGE,"E10.1.4"),sQuery(id+"F0.wireOp",EDGE,"E10.1.6"),sQuery(id+"F0.wireOp",EDGE,"E10.1.7"),sQuery(id+"F0.wireOp",EDGE,"E10.1.8"),sQuery(id+"F0.wireOp",EDGE,"E10.1.9"),sQuery(id+"F0.wireOp",EDGE,"E10.1.10"),sQuery(id+"F0.wireOp",EDGE,"E10.2.0"),sQuery(id+"F0.wireOp",EDGE,"E10.2.1"),sQuery(id+"F0.wireOp",EDGE,"E10.2.2"),sQuery(id+"F0.wireOp",EDGE,"E10.2.4"),sQuery(id+"F0.wireOp",EDGE,"E10.2.6"),sQuery(id+"F0.wireOp",EDGE,"E10.2.7"),sQuery(id+"F0.wireOp",EDGE,"E10.2.8"),sQuery(id+"F0.wireOp",EDGE,"E10.2.9"),sQuery(id+"F0.wireOp",EDGE,"E10.2.10"),sQuery(id+"F0.wireOp",EDGE,"E10.3.0"),sQuery(id+"F0.wireOp",EDGE,"E10.3.1"),sQuery(id+"F0.wireOp",EDGE,"E10.3.2"),sQuery(id+"F0.wireOp",EDGE,"E10.3.4"),sQuery(id+"F0.wireOp",EDGE,"E10.3.6"),sQuery(id+"F0.wireOp",EDGE,"E10.3.7"),sQuery(id+"F0.wireOp",EDGE,"E10.3.8"),sQuery(id+"F0.wireOp",EDGE,"E10.3.9"),sQuery(id+"F0.wireOp",EDGE,"E10.3.10")])],"isStart":false})]});}
            fillet(context, id + "F5", {"entities" : qUnion([Q0, Q1, Q2, Q3, Q4, Q5, Q6, Q7, Q8, Q9, Q10, Q11, Q12, Q13]), "radius" : 1.5 * mm, "tangentPropagation" : true, "allowEdgeOverflow" : false});
        }
    });
